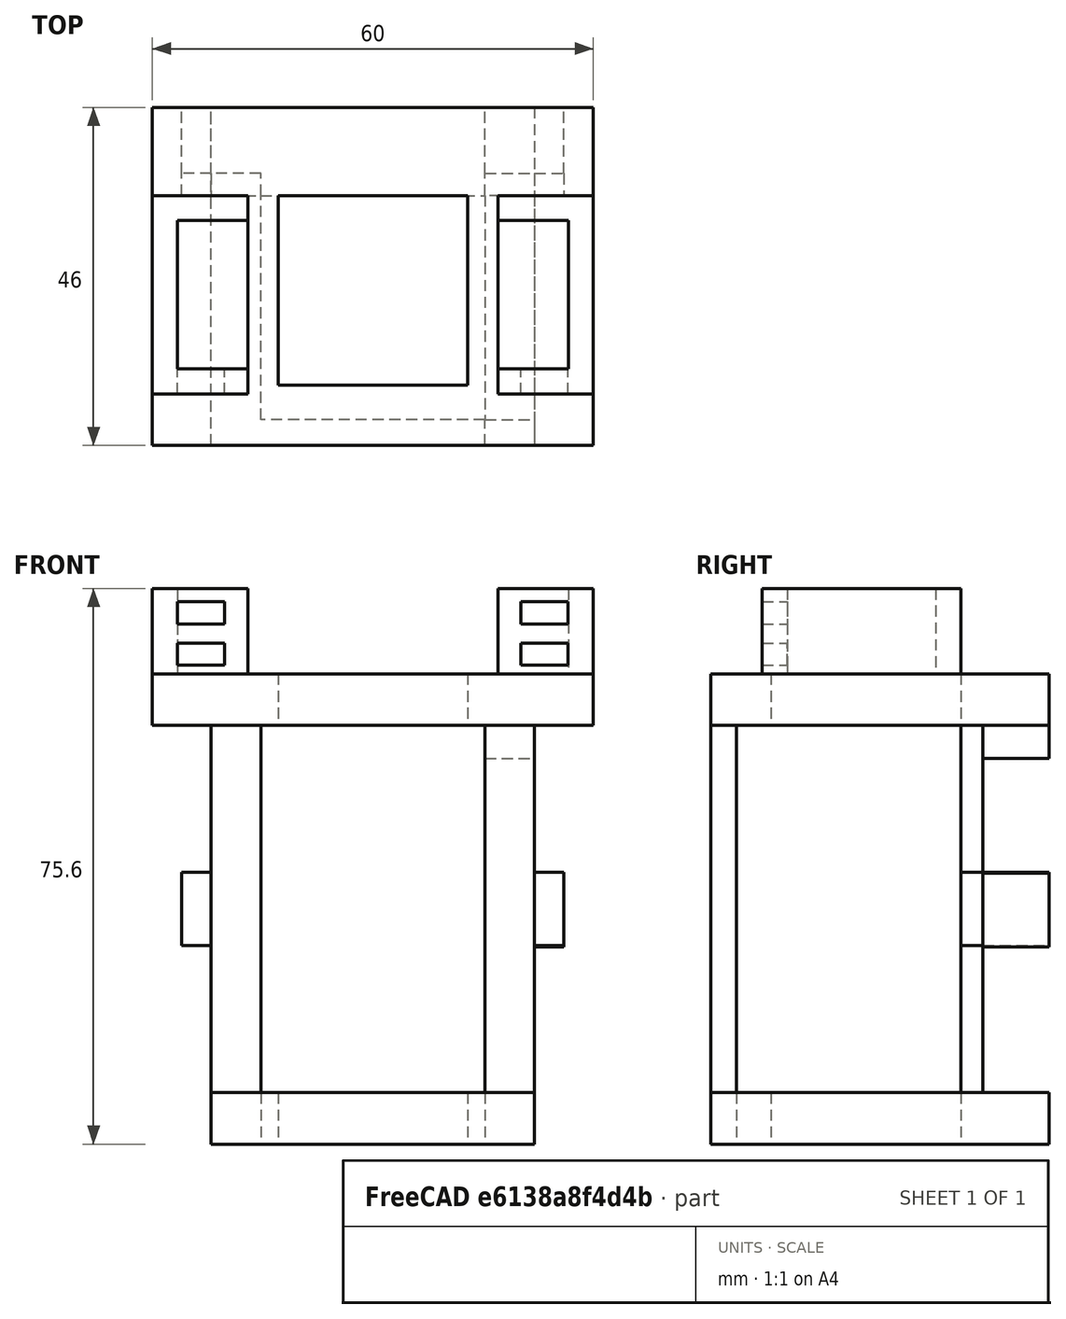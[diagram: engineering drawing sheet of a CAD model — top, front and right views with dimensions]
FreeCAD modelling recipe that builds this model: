
FCSTD DOCUMENT  (FreeCAD 0.17R13541 (Git))
Label: RFID_IR_HOLDER
License: All rights reserved
LicenseURL: http://en.wikipedia.org/wiki/All_rights_reserved
objects: Sketcher::SketchObject×22, PartDesign::Pad×14, PartDesign::Pocket×8, Mesh::Feature×6
note: 66 computed .brp shape members not serialized (recipe doc carries the construction recipe); baked Part::Feature solids carry a one-line shape summary decoded from their .brp

FEATURE [Sketcher::SketchObject] Sketch
  MapMode = 5
  sketch-geometry (4):
    g0: LineSegment StartX=-44 StartY=0 StartZ=0 EndX=0 EndY=0 EndZ=0
    g1: LineSegment StartX=0 StartY=0 StartZ=0 EndX=0 EndY=-46 EndZ=0
    g2: LineSegment StartX=0 StartY=-46 StartZ=0 EndX=-44 EndY=-46 EndZ=0
    g3: LineSegment StartX=-44 StartY=-46 StartZ=0 EndX=-44 EndY=0 EndZ=0
  constraints (12):
    c: Coincident(g0,g1)
    c: Coincident(g1,g2)
    c: Coincident(g2,g3)
    c: Coincident(g3,g0)
    c: Horizontal(g0)
    c: Horizontal(g2)
    c: Vertical(g1)
    c: Vertical(g3)
    c: Distance(g0) = 44
    c: Distance(g1) = 46
    c: DistanceX(g-1,g0) = 0
    c: DistanceY(g-1,g0) = 0
FEATURE [PartDesign::Pad] Pad
  Length = 7
  Length2 = 100
  Profile = -> Sketch
  Type = 0
FEATURE [Sketcher::SketchObject] Sketch001
  MapMode = 5
  Placement = pos=(0,0,7) rot=(0,0,1;0rad)
  Support = -> [Pad]
  sketch-geometry (4):
    g0: LineSegment StartX=-34.9 StartY=-12 StartZ=0 EndX=-9.1 EndY=-12 EndZ=0
    g1: LineSegment StartX=-9.1 StartY=-12 StartZ=0 EndX=-9.1 EndY=-37.8 EndZ=0
    g2: LineSegment StartX=-9.1 StartY=-37.8 StartZ=0 EndX=-34.9 EndY=-37.8 EndZ=0
    g3: LineSegment StartX=-34.9 StartY=-37.8 StartZ=0 EndX=-34.9 EndY=-12 EndZ=0
  constraints (12):
    c: Coincident(g0,g1)
    c: Coincident(g1,g2)
    c: Coincident(g2,g3)
    c: Coincident(g3,g0)
    c: Horizontal(g0)
    c: Horizontal(g2)
    c: Vertical(g1)
    c: Vertical(g3)
    c: Distance(g0) = 25.8
    c: Equal(g1,g0)
    c: DistanceX(g-1,g0) = -9.1
    c: DistanceY(g-1,g0) = -12
FEATURE [PartDesign::Pocket] Pocket
  Length = 8
  Length2 = 100
  Profile = -> Sketch001
  Type = 0
FEATURE [Sketcher::SketchObject] Sketch002
  MapMode = 5
  Placement = pos=(0,0,7) rot=(0,0,1;0rad)
  Support = -> [Pocket]
  sketch-geometry (4):
    g0: LineSegment StartX=-44 StartY=-12 StartZ=0 EndX=-37.25 EndY=-12 EndZ=0
    g1: LineSegment StartX=-37.25 StartY=-12 StartZ=0 EndX=-37.25 EndY=-9 EndZ=0
    g2: LineSegment StartX=-37.25 StartY=-9 StartZ=0 EndX=-44 EndY=-9 EndZ=0
    g3: LineSegment StartX=-44 StartY=-9 StartZ=0 EndX=-44 EndY=-12 EndZ=0
  constraints (12):
    c: Coincident(g0,g1)
    c: Coincident(g1,g2)
    c: Coincident(g2,g3)
    c: Coincident(g3,g0)
    c: Horizontal(g0)
    c: Horizontal(g2)
    c: Vertical(g1)
    c: Vertical(g3)
    c: Distance(g0) = 6.75
    c: Distance(g1) = 3
    c: DistanceY(g-1,g0) = -12
    c: DistanceX(g-1,g2) = -44
FEATURE [PartDesign::Pad] Pad001
  Length = 50
  Length2 = 100
  Profile = -> Sketch002
  Type = 0
FEATURE [Sketcher::SketchObject] Sketch003
  MapMode = 5
  Placement = pos=(0,0,7) rot=(0,0,1;0rad)
  Support = -> [Pad001]
  sketch-geometry (4):
    g0: LineSegment StartX=-6.75 StartY=-9 StartZ=0 EndX=0 EndY=-9 EndZ=0
    g1: LineSegment StartX=0 StartY=-9 StartZ=0 EndX=0 EndY=-12 EndZ=0
    g2: LineSegment StartX=0 StartY=-12 StartZ=0 EndX=-6.75 EndY=-12 EndZ=0
    g3: LineSegment StartX=-6.75 StartY=-12 StartZ=0 EndX=-6.75 EndY=-9 EndZ=0
  constraints (12):
    c: Coincident(g0,g1)
    c: Coincident(g1,g2)
    c: Coincident(g2,g3)
    c: Coincident(g3,g0)
    c: Horizontal(g0)
    c: Horizontal(g2)
    c: Vertical(g1)
    c: Vertical(g3)
    c: DistanceX(g-1,g0) = 0
    c: Distance(g0) = 6.75
    c: Distance(g3) = 3
    c: DistanceY(g-1,g1) = -12
FEATURE [PartDesign::Pad] Pad002
  Length = 50
  Length2 = 100
  Profile = -> Sketch003
  Type = 0
FEATURE [Sketcher::SketchObject] Sketch005
  MapMode = 5
  Placement = pos=(-6.75,0,0) rot=(0.57735,-0.57735,-0.57735;2.0944rad)
  Support = -> [Pad002]
  sketch-geometry (4):
    g0: LineSegment StartX=0 StartY=57 StartZ=0 EndX=6.75 EndY=57 EndZ=0
    g1: LineSegment StartX=6.75 StartY=57 StartZ=0 EndX=6.75 EndY=52.5 EndZ=0
    g2: LineSegment StartX=6.75 StartY=52.5 StartZ=0 EndX=0 EndY=52.5 EndZ=0
    g3: LineSegment StartX=0 StartY=52.5 StartZ=0 EndX=0 EndY=57 EndZ=0
  constraints (12):
    c: Coincident(g0,g1)
    c: Coincident(g1,g2)
    c: Coincident(g2,g3)
    c: Coincident(g3,g0)
    c: Horizontal(g0)
    c: Horizontal(g2)
    c: Vertical(g1)
    c: Vertical(g3)
    c: PointOnObject(g0,g-2)
    c: Distance(g0) = 6.75
    c: Distance(g1) = 4.5
    c: DistanceY(g-1,g0) = 57
FEATURE [PartDesign::Pad] Pad003
  Length = 9
  Length2 = 100
  Profile = -> Sketch005
  Type = 0
FEATURE [Sketcher::SketchObject] Sketch006
  MapMode = 5
  Placement = pos=(0,-9,0) rot=(0,0.707107,0.707107;3.14159rad)
  Support = -> [Pad001]
  sketch-geometry (4):
    g0: LineSegment StartX=37.25 StartY=57 StartZ=0 EndX=44 EndY=57 EndZ=0
    g1: LineSegment StartX=44 StartY=57 StartZ=0 EndX=44 EndY=52.5 EndZ=0
    g2: LineSegment StartX=44 StartY=52.5 StartZ=0 EndX=37.25 EndY=52.5 EndZ=0
    g3: LineSegment StartX=37.25 StartY=52.5 StartZ=0 EndX=37.25 EndY=57 EndZ=0
  constraints (12):
    c: Coincident(g0,g1)
    c: Coincident(g1,g2)
    c: Coincident(g2,g3)
    c: Coincident(g3,g0)
    c: Horizontal(g0)
    c: Horizontal(g2)
    c: Vertical(g1)
    c: Vertical(g3)
    c: DistanceX(g-1,g0) = 44
    c: Distance(g0) = 6.75
    c: Distance(g3) = 4.5
    c: DistanceY(g-1,g0) = 57
FEATURE [Sketcher::SketchObject] Sketch008
  MapMode = 5
  Placement = pos=(0,0,0) rot=(0.57735,0.57735,0.57735;2.0944rad)
  sketch-geometry (4):
    g0: LineSegment StartX=-12 StartY=37 StartZ=0 EndX=-9 EndY=37 EndZ=0
    g1: LineSegment StartX=-9 StartY=37 StartZ=0 EndX=-9 EndY=27 EndZ=0
    g2: LineSegment StartX=-9 StartY=27 StartZ=0 EndX=-12 EndY=27 EndZ=0
    g3: LineSegment StartX=-12 StartY=27 StartZ=0 EndX=-12 EndY=37 EndZ=0
  constraints (12):
    c: Coincident(g0,g1)
    c: Coincident(g1,g2)
    c: Coincident(g2,g3)
    c: Coincident(g3,g0)
    c: Horizontal(g0)
    c: Horizontal(g2)
    c: Vertical(g1)
    c: Vertical(g3)
    c: Distance(g1) = 10
    c: Distance(g0) = 3
    c: DistanceX(g-1,g1) = -9
    c: DistanceY(g-1,g1) = 27
FEATURE [PartDesign::Pad] Pad006
  Length = 4
  Length2 = 100
  Placement = pos=(0,0,0) rot=(0.57735,0.57735,0.57735;2.0944rad)
  Profile = -> Sketch008
  Type = 0
FEATURE [Sketcher::SketchObject] Sketch009
  MapMode = 5
  Placement = pos=(0,-9,0) rot=(0,0.707107,0.707107;3.14159rad)
  Support = -> [Pad006]
  sketch-geometry (4):
    g0: LineSegment StartX=-4 StartY=37 StartZ=0 EndX=0 EndY=37 EndZ=0
    g1: LineSegment StartX=0 StartY=37 StartZ=0 EndX=0 EndY=27 EndZ=0
    g2: LineSegment StartX=0 StartY=27 StartZ=0 EndX=-4 EndY=27 EndZ=0
    g3: LineSegment StartX=-4 StartY=27 StartZ=0 EndX=-4 EndY=37 EndZ=0
  constraints (13):
    c: Coincident(g0,g1)
    c: Coincident(g1,g2)
    c: Coincident(g2,g3)
    c: Coincident(g3,g0)
    c: Horizontal(g0)
    c: Horizontal(g2)
    c: Vertical(g1)
    c: Vertical(g3)
    c: PointOnObject(g1,g-2)
    c: Distance(g0) = 4
    c: Distance(g3) = 10
    c: DistanceX(g-1,g1) = 0
    c: DistanceY(g-1,g1) = 27
FEATURE [PartDesign::Pad] Pad007
  Length = 9
  Length2 = 100
  Profile = -> Sketch009
  Type = 0
FEATURE [Sketcher::SketchObject] Sketch010
  MapMode = 5
  Placement = pos=(0,-9,0) rot=(0,0.707107,0.707107;3.14159rad)
  sketch-geometry (4):
    g0: LineSegment StartX=44 StartY=37 StartZ=0 EndX=48 EndY=37 EndZ=0
    g1: LineSegment StartX=48 StartY=37 StartZ=0 EndX=48 EndY=27 EndZ=0
    g2: LineSegment StartX=48 StartY=27 StartZ=0 EndX=44 EndY=27 EndZ=0
    g3: LineSegment StartX=44 StartY=27 StartZ=0 EndX=44 EndY=37 EndZ=0
  constraints (12):
    c: Coincident(g0,g1)
    c: Coincident(g1,g2)
    c: Coincident(g2,g3)
    c: Coincident(g3,g0)
    c: Horizontal(g0)
    c: Horizontal(g2)
    c: Vertical(g1)
    c: Vertical(g3)
    c: Distance(g0) = 4
    c: Distance(g1) = 10
    c: DistanceX(g-1,g2) = 44
    c: DistanceY(g-1,g2) = 27
FEATURE [PartDesign::Pad] Pad008
  Length = 9
  Length2 = 100
  Placement = pos=(0,-9,0) rot=(0,0.707107,0.707107;3.14159rad)
  Profile = -> Sketch010
  Type = 0
FEATURE [Sketcher::SketchObject] Sketch011
  MapMode = 5
  Placement = pos=(0,0,57) rot=(0,0,1;0rad)
  Support = -> [Pad003]
  sketch-geometry (4):
    g0: LineSegment StartX=-52 StartY=0 StartZ=0 EndX=8 EndY=0 EndZ=0
    g1: LineSegment StartX=8 StartY=0 StartZ=0 EndX=8 EndY=-46 EndZ=0
    g2: LineSegment StartX=8 StartY=-46 StartZ=0 EndX=-52 EndY=-46 EndZ=0
    g3: LineSegment StartX=-52 StartY=-46 StartZ=0 EndX=-52 EndY=0 EndZ=0
  constraints (12):
    c: Coincident(g0,g1)
    c: Coincident(g1,g2)
    c: Coincident(g2,g3)
    c: Coincident(g3,g0)
    c: Horizontal(g0)
    c: Horizontal(g2)
    c: Vertical(g1)
    c: Vertical(g3)
    c: DistanceY(g-1,g0) = 0
    c: Distance(g0) = 60
    c: Distance(g3) = 46
    c: DistanceX(g-1,g0) = -52
FEATURE [PartDesign::Pad] Pad009
  Length = 7
  Length2 = 100
  Profile = -> Sketch011
  Type = 0
FEATURE [Sketcher::SketchObject] Sketch012
  MapMode = 5
  Placement = pos=(0,0,64) rot=(0,0,1;0rad)
  Support = -> [Pad009]
  sketch-geometry (4):
    g0: LineSegment StartX=-34.9 StartY=-12 StartZ=0 EndX=-9.1 EndY=-12 EndZ=0
    g1: LineSegment StartX=-9.1 StartY=-12 StartZ=0 EndX=-9.1 EndY=-37.8 EndZ=0
    g2: LineSegment StartX=-9.1 StartY=-37.8 StartZ=0 EndX=-34.9 EndY=-37.8 EndZ=0
    g3: LineSegment StartX=-34.9 StartY=-37.8 StartZ=0 EndX=-34.9 EndY=-12 EndZ=0
  constraints (12):
    c: Coincident(g0,g1)
    c: Coincident(g1,g2)
    c: Coincident(g2,g3)
    c: Coincident(g3,g0)
    c: Horizontal(g0)
    c: Horizontal(g2)
    c: Vertical(g1)
    c: Vertical(g3)
    c: Distance(g0) = 25.8
    c: Distance(g3) = 25.8
    c: DistanceY(g-1,g0) = -12
    c: DistanceX(g-1,g0) = -9.1
FEATURE [PartDesign::Pocket] Pocket001
  Length = 7
  Length2 = 100
  Profile = -> Sketch012
  Type = 0
FEATURE [Sketcher::SketchObject] Sketch013
  MapMode = 5
  Placement = pos=(0,0,7) rot=(0,0,1;0rad)
  Support = -> [Pocket]
  sketch-geometry (4):
    g0: LineSegment StartX=-6.75 StartY=-42.5 StartZ=0 EndX=0 EndY=-42.5 EndZ=0
    g1: LineSegment StartX=0 StartY=-42.5 StartZ=0 EndX=0 EndY=-46 EndZ=0
    g2: LineSegment StartX=0 StartY=-46 StartZ=0 EndX=-6.75 EndY=-46 EndZ=0
    g3: LineSegment StartX=-6.75 StartY=-46 StartZ=0 EndX=-6.75 EndY=-42.5 EndZ=0
  constraints (13):
    c: Coincident(g0,g1)
    c: Coincident(g1,g2)
    c: Coincident(g2,g3)
    c: Coincident(g3,g0)
    c: Horizontal(g0)
    c: Horizontal(g2)
    c: Vertical(g1)
    c: Vertical(g3)
    c: PointOnObject(g1,g-2)
    c: Distance(g0) = 6.75
    c: Distance(g3) = 3.5
    c: DistanceX(g-1,g0) = 0
    c: DistanceY(g-1,g0) = -42.5
FEATURE [PartDesign::Pad] Pad010
  Length = 50
  Length2 = 100
  Profile = -> Sketch013
  Type = 0
FEATURE [Sketcher::SketchObject] Sketch014
  MapMode = 5
  Placement = pos=(0,0,7) rot=(0,0,1;0rad)
  Support = -> [Pad001]
  sketch-geometry (4):
    g0: LineSegment StartX=-44 StartY=-42.5 StartZ=0 EndX=-37.25 EndY=-42.5 EndZ=0
    g1: LineSegment StartX=-37.25 StartY=-42.5 StartZ=0 EndX=-37.25 EndY=-46 EndZ=0
    g2: LineSegment StartX=-37.25 StartY=-46 StartZ=0 EndX=-44 EndY=-46 EndZ=0
    g3: LineSegment StartX=-44 StartY=-46 StartZ=0 EndX=-44 EndY=-42.5 EndZ=0
  constraints (12):
    c: Coincident(g0,g1)
    c: Coincident(g1,g2)
    c: Coincident(g2,g3)
    c: Coincident(g3,g0)
    c: Horizontal(g0)
    c: Horizontal(g2)
    c: Vertical(g1)
    c: Vertical(g3)
    c: Distance(g0) = 6.75
    c: Distance(g3) = 3.5
    c: DistanceX(g-1,g2) = -44
    c: DistanceY(g-1,g2) = -46
FEATURE [Sketcher::SketchObject] Sketch015
  MapMode = 5
  Placement = pos=(0,0,64) rot=(0,0,1;0rad)
  Support = -> [Pocket001]
  sketch-geometry (4):
    g0: LineSegment StartX=-5 StartY=-12 StartZ=0 EndX=8 EndY=-12 EndZ=0
    g1: LineSegment StartX=8 StartY=-12 StartZ=0 EndX=8 EndY=-39 EndZ=0
    g2: LineSegment StartX=8 StartY=-39 StartZ=0 EndX=-5 EndY=-39 EndZ=0
    g3: LineSegment StartX=-5 StartY=-39 StartZ=0 EndX=-5 EndY=-12 EndZ=0
  constraints (12):
    c: Coincident(g0,g1)
    c: Coincident(g1,g2)
    c: Coincident(g2,g3)
    c: Coincident(g3,g0)
    c: Horizontal(g0)
    c: Horizontal(g2)
    c: Vertical(g1)
    c: Vertical(g3)
    c: Distance(g0) = 13
    c: Distance(g1) = 27
    c: DistanceX(g-1,g0) = 8
    c: DistanceY(g-1,g0) = -12
FEATURE [PartDesign::Pad] Pad012
  Length = 11.6
  Length2 = 100
  Profile = -> Sketch015
  Type = 0
FEATURE [Sketcher::SketchObject] Sketch016
  MapMode = 5
  Placement = pos=(0,0,64) rot=(0,0,1;0rad)
  Support = -> [Pad012]
  sketch-geometry (4):
    g0: LineSegment StartX=-52 StartY=-12 StartZ=0 EndX=-39 EndY=-12 EndZ=0
    g1: LineSegment StartX=-39 StartY=-12 StartZ=0 EndX=-39 EndY=-39 EndZ=0
    g2: LineSegment StartX=-39 StartY=-39 StartZ=0 EndX=-52 EndY=-39 EndZ=0
    g3: LineSegment StartX=-52 StartY=-39 StartZ=0 EndX=-52 EndY=-12 EndZ=0
  constraints (12):
    c: Coincident(g0,g1)
    c: Coincident(g1,g2)
    c: Coincident(g2,g3)
    c: Coincident(g3,g0)
    c: Horizontal(g0)
    c: Horizontal(g2)
    c: Vertical(g1)
    c: Vertical(g3)
    c: Distance(g0) = 13
    c: Distance(g3) = 27
    c: DistanceY(g-1,g0) = -12
    c: DistanceX(g-1,g0) = -52
FEATURE [PartDesign::Pad] Pad013
  Length = 11.6
  Length2 = 100
  Profile = -> Sketch016
  Type = 0
FEATURE [Sketcher::SketchObject] Sketch017
  MapMode = 5
  Placement = pos=(0,0,75.6) rot=(0,0,1;0rad)
  Support = -> [Pad013]
  sketch-geometry (4):
    g0: LineSegment StartX=-5 StartY=-15.4 StartZ=0 EndX=4.6 EndY=-15.4 EndZ=0
    g1: LineSegment StartX=4.6 StartY=-15.4 StartZ=0 EndX=4.6 EndY=-35.6 EndZ=0
    g2: LineSegment StartX=4.6 StartY=-35.6 StartZ=0 EndX=-5 EndY=-35.6 EndZ=0
    g3: LineSegment StartX=-5 StartY=-35.6 StartZ=0 EndX=-5 EndY=-15.4 EndZ=0
  constraints (12):
    c: Coincident(g0,g1)
    c: Coincident(g1,g2)
    c: Coincident(g2,g3)
    c: Coincident(g3,g0)
    c: Horizontal(g0)
    c: Horizontal(g2)
    c: Vertical(g1)
    c: Vertical(g3)
    c: DistanceY(g-1,g0) = -15.4
    c: DistanceX(g-1,g0) = 4.6
    c: Distance(g3) = 20.2
    c: Distance(g0) = 9.6
FEATURE [PartDesign::Pocket] Pocket002
  Length = 11.6
  Length2 = 100
  Profile = -> Sketch017
  Type = 0
FEATURE [Sketcher::SketchObject] Sketch018
  MapMode = 5
  Placement = pos=(0,0,75.6) rot=(0,0,1;0rad)
  Support = -> [Pocket002]
  sketch-geometry (4):
    g0: LineSegment StartX=-48.6 StartY=-15.4 StartZ=0 EndX=-39 EndY=-15.4 EndZ=0
    g1: LineSegment StartX=-39 StartY=-15.4 StartZ=0 EndX=-39 EndY=-35.6 EndZ=0
    g2: LineSegment StartX=-39 StartY=-35.6 StartZ=0 EndX=-48.6 EndY=-35.6 EndZ=0
    g3: LineSegment StartX=-48.6 StartY=-35.6 StartZ=0 EndX=-48.6 EndY=-15.4 EndZ=0
  constraints (12):
    c: Coincident(g0,g1)
    c: Coincident(g1,g2)
    c: Coincident(g2,g3)
    c: Coincident(g3,g0)
    c: Horizontal(g0)
    c: Horizontal(g2)
    c: Vertical(g1)
    c: Vertical(g3)
    c: DistanceX(g-1,g0) = -48.6
    c: DistanceY(g-1,g0) = -15.4
    c: Distance(g0) = 9.6
    c: Distance(g1) = 20.2
FEATURE [PartDesign::Pocket] Pocket003
  Length = 11.6
  Length2 = 100
  Profile = -> Sketch018
  Type = 0
FEATURE [Sketcher::SketchObject] Sketch019
  MapMode = 5
  Placement = pos=(0,-39,0) rot=(1,0,0;1.5708rad)
  Support = -> [Pocket003]
  sketch-geometry (4):
    g0: LineSegment StartX=-48.6 StartY=73.8 StartZ=0 EndX=-42.2 EndY=73.8 EndZ=0
    g1: LineSegment StartX=-42.2 StartY=73.8 StartZ=0 EndX=-42.2 EndY=70.8 EndZ=0
    g2: LineSegment StartX=-42.2 StartY=70.8 StartZ=0 EndX=-48.6 EndY=70.8 EndZ=0
    g3: LineSegment StartX=-48.6 StartY=70.8 StartZ=0 EndX=-48.6 EndY=73.8 EndZ=0
  constraints (12):
    c: Coincident(g0,g1)
    c: Coincident(g1,g2)
    c: Coincident(g2,g3)
    c: Coincident(g3,g0)
    c: Horizontal(g0)
    c: Horizontal(g2)
    c: Vertical(g1)
    c: Vertical(g3)
    c: Distance(g0) = 6.4
    c: Distance(g1) = 3
    c: DistanceY(g-1,g0) = 73.8
    c: DistanceX(g-1,g2) = -48.6
FEATURE [PartDesign::Pocket] Pocket004
  Length = 5
  Length2 = 100
  Profile = -> Sketch019
  Type = 0
FEATURE [Sketcher::SketchObject] Sketch021
  MapMode = 5
  Placement = pos=(0,-39,0) rot=(1,0,0;1.5708rad)
  Support = -> [Pocket004]
  sketch-geometry (4):
    g0: LineSegment StartX=-48.6 StartY=65.2 StartZ=0 EndX=-42.2 EndY=65.2 EndZ=0
    g1: LineSegment StartX=-42.2 StartY=65.2 StartZ=0 EndX=-42.2 EndY=68.2 EndZ=0
    g2: LineSegment StartX=-42.2 StartY=68.2 StartZ=0 EndX=-48.6 EndY=68.2 EndZ=0
    g3: LineSegment StartX=-48.6 StartY=68.2 StartZ=0 EndX=-48.6 EndY=65.2 EndZ=0
  constraints (12):
    c: Coincident(g0,g1)
    c: Coincident(g1,g2)
    c: Coincident(g2,g3)
    c: Coincident(g3,g0)
    c: Horizontal(g0)
    c: Horizontal(g2)
    c: Vertical(g1)
    c: Vertical(g3)
    c: DistanceX(g-1,g0) = -48.6
    c: Distance(g0) = 6.4
    c: Distance(g1) = 3
    c: DistanceY(g-1,g2) = 68.2
FEATURE [PartDesign::Pocket] Pocket005
  Length = 5
  Length2 = 100
  Profile = -> Sketch021
  Type = 0
FEATURE [Sketcher::SketchObject] Sketch022
  MapMode = 5
  Placement = pos=(0,-39,0) rot=(1,0,0;1.5708rad)
  Support = -> [Pocket005]
  sketch-geometry (4):
    g0: LineSegment StartX=-1.85 StartY=73.8 StartZ=0 EndX=4.55 EndY=73.8 EndZ=0
    g1: LineSegment StartX=4.55 StartY=73.8 StartZ=0 EndX=4.55 EndY=70.8 EndZ=0
    g2: LineSegment StartX=4.55 StartY=70.8 StartZ=0 EndX=-1.85 EndY=70.8 EndZ=0
    g3: LineSegment StartX=-1.85 StartY=70.8 StartZ=0 EndX=-1.85 EndY=73.8 EndZ=0
  constraints (12):
    c: Coincident(g0,g1)
    c: Coincident(g1,g2)
    c: Coincident(g2,g3)
    c: Coincident(g3,g0)
    c: Horizontal(g0)
    c: Horizontal(g2)
    c: Vertical(g1)
    c: Vertical(g3)
    c: Distance(g0) = 6.4
    c: Distance(g3) = 3
    c: DistanceY(g-1,g0) = 73.8
    c: DistanceX(g-1,g0) = -1.85
FEATURE [PartDesign::Pocket] Pocket006
  Length = 5
  Length2 = 100
  Profile = -> Sketch022
  Type = 0
FEATURE [Sketcher::SketchObject] Sketch023
  MapMode = 5
  Placement = pos=(0,-39,0) rot=(1,0,0;1.5708rad)
  Support = -> [Pocket006]
  sketch-geometry (4):
    g0: LineSegment StartX=-1.85 StartY=68.2 StartZ=0 EndX=4.55 EndY=68.2 EndZ=0
    g1: LineSegment StartX=4.55 StartY=68.2 StartZ=0 EndX=4.55 EndY=65.2 EndZ=0
    g2: LineSegment StartX=4.55 StartY=65.2 StartZ=0 EndX=-1.85 EndY=65.2 EndZ=0
    g3: LineSegment StartX=-1.85 StartY=65.2 StartZ=0 EndX=-1.85 EndY=68.2 EndZ=0
  constraints (12):
    c: Coincident(g0,g1)
    c: Coincident(g1,g2)
    c: Coincident(g2,g3)
    c: Coincident(g3,g0)
    c: Horizontal(g0)
    c: Horizontal(g2)
    c: Vertical(g1)
    c: Vertical(g3)
    c: Distance(g0) = 6.4
    c: Distance(g1) = 3
    c: DistanceX(g-1,g0) = -1.85
    c: DistanceY(g-1,g0) = 68.2
FEATURE [PartDesign::Pocket] Pocket007
  Length = 5
  Length2 = 100
  Profile = -> Sketch023
  Type = 0
FEATURE [PartDesign::Pad] Pad014
  Length = 50
  Length2 = 100
  Profile = -> Sketch014
  Type = 0
FEATURE [Sketcher::SketchObject] Sketch024
  MapMode = 5
  Placement = pos=(0,0,7) rot=(0,0,1;0rad)
  Support = -> [Pad007]
  sketch-geometry (4):
    g0: LineSegment StartX=-6.75 StartY=-42.5 StartZ=0 EndX=0 EndY=-42.5 EndZ=0
    g1: LineSegment StartX=0 StartY=-42.5 StartZ=0 EndX=0 EndY=-46 EndZ=0
    g2: LineSegment StartX=0 StartY=-46 StartZ=0 EndX=-6.75 EndY=-46 EndZ=0
    g3: LineSegment StartX=-6.75 StartY=-46 StartZ=0 EndX=-6.75 EndY=-42.5 EndZ=0
  constraints (12):
    c: Coincident(g0,g1)
    c: Coincident(g1,g2)
    c: Coincident(g2,g3)
    c: Coincident(g3,g0)
    c: Horizontal(g0)
    c: Horizontal(g2)
    c: Vertical(g1)
    c: Vertical(g3)
    c: Distance(g0) = 6.75
    c: Distance(g1) = 3.5
    c: DistanceY(g-1,g1) = -46
    c: DistanceX(g-1,g1) = 0
FEATURE [PartDesign::Pad] Pad016
  Length = 50
  Length2 = 100
  Profile = -> Sketch024
  Type = 0
FEATURE [PartDesign::Pad] Pad017
  Length = 9
  Length2 = 100
  Profile = -> Sketch006
  Type = 0
FEATURE [Mesh::Feature] Mesh  label="Pad008 (Meshed)"
FEATURE [Mesh::Feature] Mesh001  label="Pocket007 (Meshed)"
FEATURE [Mesh::Feature] Mesh002  label="Pad014 (Meshed)"
FEATURE [Mesh::Feature] Mesh003  label="Pad016 (Meshed)"
FEATURE [Mesh::Feature] Mesh004  label="Pad017 (Meshed)"
FEATURE [Mesh::Feature] Mesh005
